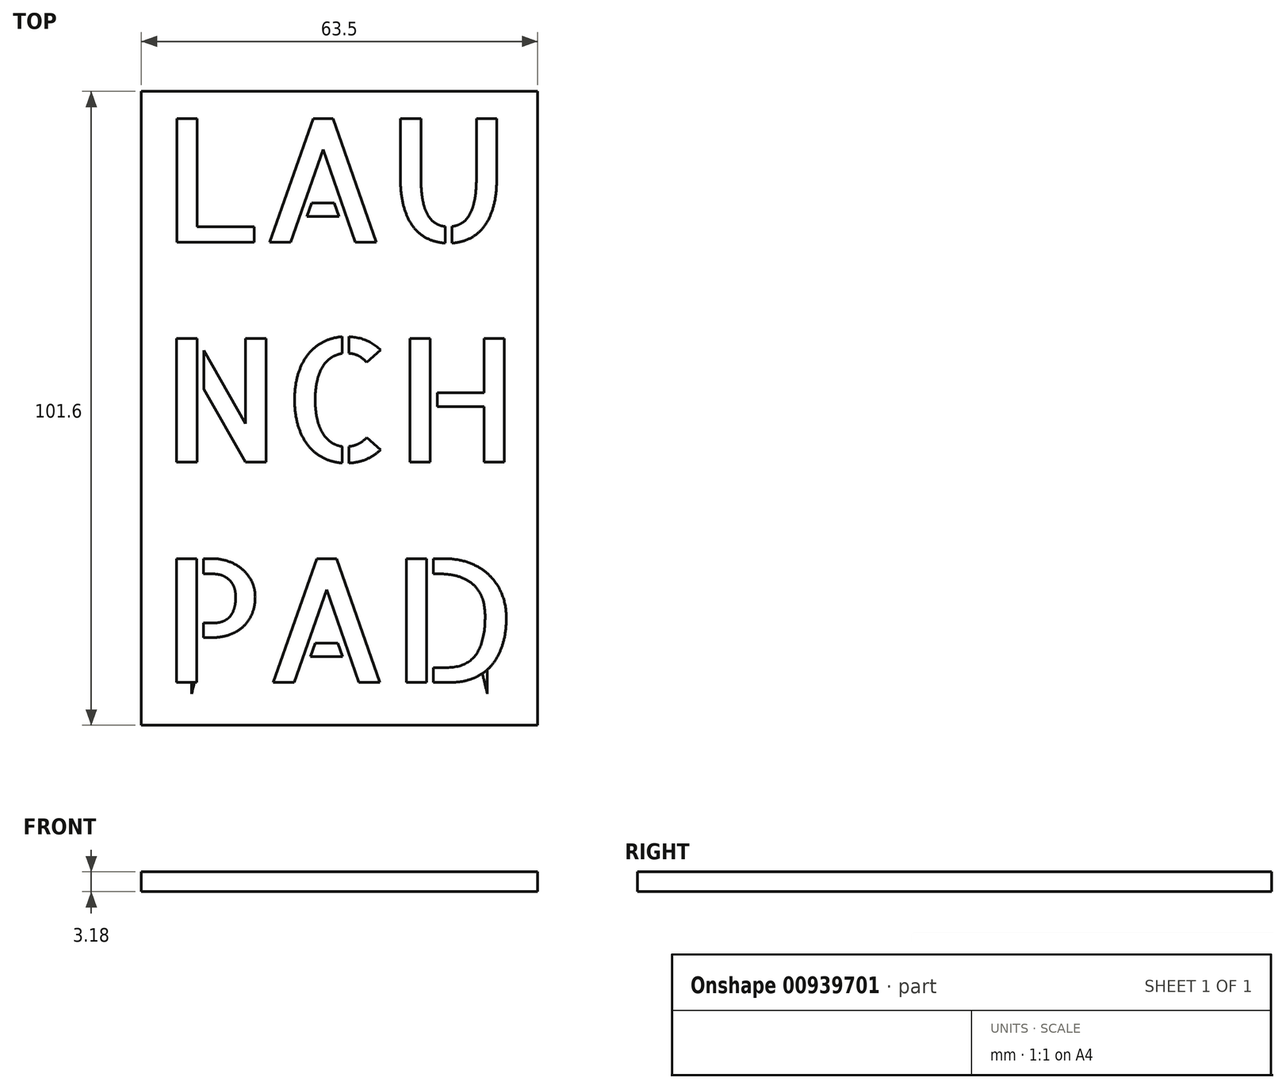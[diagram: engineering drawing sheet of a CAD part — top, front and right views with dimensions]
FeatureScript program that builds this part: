
annotation { "Feature Type Name" : "Feature", "Feature Type Description" : "" }
export const myFeature = defineFeature(function(context is Context, id is Id, definition is map)
    precondition{}
    {
        {
            var Q0;
            Q0=qCreatedBy(makeId("Top.planeOp"),FACE);
            var sketch = newSketch(context, id + "F0", { "sketchPlane" : qUnion([Q0])});
            skLineSegment(sketch, "E0.bottom", {"start": v(-31.75, 50.8) * mm, "end": v(31.75, 50.8) * mm});
            skLineSegment(sketch, "E0.top", {"start": v(-31.75, -50.8) * mm, "end": v(31.75, -50.8) * mm});
            skLineSegment(sketch, "E0.left", {"start": v(-31.75, 50.8) * mm, "end": v(-31.75, -50.8) * mm});
            skLineSegment(sketch, "E0.right", {"start": v(31.75, 50.8) * mm, "end": v(31.75, -50.8) * mm});
            skSolve(sketch);
        }
        {
            var Q0;
            Q0=makeQuery(id+"F0.imprint","IMPRINT",FACE,{"disambiguationData":[TD([[makeQuery(id+"F0.imprint","IMPRINT",EDGE,{"derivedFrom":sQuery(id+"F0.wireOp",EDGE,"E0.bottom")}),-1.0]])]});
            extrude(context, id + "F1", {"entities" : qUnion([Q0]), "depth" : 3.17 * mm, "offsetDistance" : 25.4 * mm});
        }
        {
            var Q0;
            Q0=makeQuery(id+"F1.opExtrude","CAP_FACE",FACE,{"disambiguationData":[OSD([sQuery(id+"F0.wireOp",EDGE,"E0.bottom"),sQuery(id+"F0.wireOp",EDGE,"E0.top"),sQuery(id+"F0.wireOp",EDGE,"E0.left"),sQuery(id+"F0.wireOp",EDGE,"E0.right")])],"isStart":false});
            var sketch = newSketch(context, id + "F2", { "sketchPlane" : qUnion([Q0])});
            skText(sketch, "E1", { "text": "LAU\nNCH\nPAD", "fontName": "AllertaStencil-Regular.ttf"});
            const initialGuessF2  = {"E1": [-0.02858, 0.02662, 1, 0, 0.01984]};
            skSetInitialGuess(sketch, initialGuessF2);
            skSolve(sketch);
        }
        {
            var Q0;
            Q0 = qSketchRegion(id + "F2", true);
            extrude(context, id + "F3", {"entities" : qUnion([Q0]), "operationType" : NewBodyOperationType.ADD, "depth" : 3 / 812.8 * mm, "offsetDistance" : 25.4 * mm});
        }
        {
            var Q0;
            {var subQ0=sQuery(id+"F0.wireOp",EDGE,"E0.top");var subQ1=sQuery(id+"F0.wireOp",EDGE,"E0.right");var subQ2=sQuery(id+"F0.wireOp",EDGE,"E0.bottom");var subQ3=sQuery(id+"F0.wireOp",EDGE,"E0.left");Q0=makeQuery(id+"F3.boolean.opBoolean","SPLIT",FACE,{"disambiguationData":[TD([makeQuery(id+"F1.opExtrude","SWEPT_FACE",FACE,{"disambiguationData":[OSD([subQ2])]})])],"derivedFrom":makeQuery(id+"F1.opExtrude","CAP_FACE",FACE,{"disambiguationData":[OSD([subQ2,subQ0,subQ3,subQ1])],"isStart":false})});}
            var sketch = newSketch(context, id + "F4", { "sketchPlane" : qUnion([Q0])});
            skPoint(sketch, "E2.1.internal.snap0", {"position": v(-24.46, 11.18) * mm});
            skPoint(sketch, "E3.2.internal.snap0", {"position": v(-2.05, -39.82) * mm});
            skFitSpline(sketch, "E4", {"points": [v(-5.95, -27.35) * mm, v(-8.13, -33.72) * mm, v(-5.95, -44.95) * mm], "startDerivative": vector(-6.61, -13.3) * mm, "endDerivative": vector(6.04, -21.2) * mm});
            skFitSpline(sketch, "E5", {"points": [v(-5.95, -44.95) * mm, v(-4.62, -39.82) * mm, v(0, -49.1) * mm], "startDerivative": vector(2.52, 18.1) * mm, "endDerivative": vector(9.23, -24.14) * mm});
            skFitSpline(sketch, "E6.MirrorCS", {"points": [v(5.95, -44.95) * mm, v(4.62, -39.82) * mm, v(0, -49.1) * mm], "startDerivative": vector(-2.52, 18.1) * mm, "endDerivative": vector(-9.23, -24.14) * mm});
            skFitSpline(sketch, "E7.MirrorCS", {"points": [v(5.95, -27.35) * mm, v(8.13, -33.72) * mm, v(5.95, -44.95) * mm], "startDerivative": vector(6.61, -13.3) * mm, "endDerivative": vector(-6.04, -21.2) * mm});
            skEllipticalArc(sketch, "E8", {});
            skLineSegment(sketch, "E9", {"start": v(-5.95, -27.35) * mm, "end": v(5.95, -27.35) * mm});
            skFitSpline(sketch, "E10", {"points": [v(-11.7, -12.15) * mm, v(-20.42, -19.2) * mm, v(-23.68, -45.79) * mm], "startDerivative": vector(-25.64, -12.83) * mm, "endDerivative": vector(-0.24, -51.69) * mm});
            skFitSpline(sketch, "E11", {"points": [v(-23.68, -45.79) * mm, v(-17.31, -29.12) * mm, v(-7.77, -24.5) * mm], "startDerivative": vector(8.28, 34.86) * mm, "endDerivative": vector(24.24, 6.48) * mm});
            skFitSpline(sketch, "E12.MirrorCS", {"points": [v(11.7, -12.15) * mm, v(20.42, -19.2) * mm, v(23.68, -45.79) * mm], "startDerivative": vector(25.64, -12.83) * mm, "endDerivative": vector(0.24, -51.69) * mm});
            skFitSpline(sketch, "E13.MirrorCS", {"points": [v(23.68, -45.79) * mm, v(17.31, -29.12) * mm, v(7.77, -24.5) * mm], "startDerivative": vector(-8.28, 34.86) * mm, "endDerivative": vector(-24.24, 6.48) * mm});
            const initialGuessF4  = {"E8": [0, 0, 0, -1, 0.030929374872957237, 0.012728021231775851, 0.4860810952605146, 5.797104211919072]};
            skSetInitialGuess(sketch, initialGuessF4);
            skSolve(sketch);
        }
        {
            var Q0;
            {var subQ1=makeQuery(id+"F3.opExtrude","CAP_EDGE",EDGE,{"disambiguationData":[OSD([sQuery(id+"F2.wireOp",EDGE,"E1.sketch_text.stroke-6")])],"isStart":true});Q0=makeQuery(id+"F4.imprint","IMPRINT",FACE,{"disambiguationData":[TD([[makeQuery(id+"F4.imprint","IMPRINT",EDGE,{"derivedFrom":subQ1}),1.0]])]});}
            var Q1;
            Q1=makeQuery(id+"F4.imprint","IMPRINT",FACE,{"disambiguationData":[TD([[makeQuery(id+"F4.imprint","IMPRINT",EDGE,{"derivedFrom":makeQuery(id+"F3.opExtrude","CAP_EDGE",EDGE,{"disambiguationData":[OSD([sQuery(id+"F2.wireOp",EDGE,"E1.sketch_text.stroke-97")])],"isStart":true})}),1.0]])]});
            var Q2;
            {var subQ9=makeQuery(id+"F3.opExtrude","CAP_EDGE",EDGE,{"disambiguationData":[OSD([sQuery(id+"F2.wireOp",EDGE,"E1.sketch_text.stroke-130")])],"isStart":true});Q2=makeQuery(id+"F4.imprint","IMPRINT",FACE,{"disambiguationData":[TD([[makeQuery(id+"F4.imprint","IMPRINT",EDGE,{"derivedFrom":subQ9}),1.0]])]});}
            var Q3;
            {var subQ12=makeQuery(id+"F3.opExtrude","CAP_EDGE",EDGE,{"disambiguationData":[OSD([sQuery(id+"F2.wireOp",EDGE,"E1.sketch_text.stroke-126")])],"isStart":true});Q3=makeQuery(id+"F4.imprint","IMPRINT",FACE,{"disambiguationData":[TD([[makeQuery(id+"F4.imprint","IMPRINT",EDGE,{"derivedFrom":subQ12}),1.0]])]});}
            var Q4;
            {var subQ1=sQuery(id+"F4.wireOp",EDGE,"E7.MirrorCS");var subQ3=makeQuery(id+"F3.opExtrude","CAP_EDGE",EDGE,{"disambiguationData":[OSD([sQuery(id+"F2.wireOp",EDGE,"E1.sketch_text.stroke-125")])],"isStart":true});var subQ4=makeQuery(id+"F4.imprint","INTERSECT",VERTEX,{"derivedFrom":[subQ3,subQ1]});Q4=makeQuery(id+"F4.imprint","IMPRINT",FACE,{"disambiguationData":[TD([[makeQuery(id+"F4.imprint","IMPRINT",EDGE,{"disambiguationData":[TD([[subQ4,1.0]])],"derivedFrom":subQ3}),1.0]])]});}
            var Q5;
            {var subQ1=sQuery(id+"F4.wireOp",EDGE,"E4");var subQ3=makeQuery(id+"F3.opExtrude","CAP_EDGE",EDGE,{"disambiguationData":[OSD([sQuery(id+"F2.wireOp",EDGE,"E1.sketch_text.stroke-123")])],"isStart":true});var subQ4=makeQuery(id+"F4.imprint","INTERSECT",VERTEX,{"derivedFrom":[subQ3,subQ1]});Q5=makeQuery(id+"F4.imprint","IMPRINT",FACE,{"disambiguationData":[TD([[makeQuery(id+"F4.imprint","IMPRINT",EDGE,{"disambiguationData":[TD([[subQ4,-1.0]])],"derivedFrom":subQ3}),1.0]])]});}
            var Q6;
            {var subQ0=sQuery(id+"F4.wireOp",EDGE,"E13.MirrorCS");var subQ1=sQuery(id+"F4.wireOp",EDGE,"E12.MirrorCS");var subQ2=makeQuery(id+"F4.imprint","INTERSECT",VERTEX,{"derivedFrom":[subQ1,subQ0]});Q6=makeQuery(id+"F4.imprint","IMPRINT",FACE,{"disambiguationData":[TD([[makeQuery(id+"F4.imprint","IMPRINT",EDGE,{"disambiguationData":[TD([[subQ2,1.0]])],"derivedFrom":subQ1}),-1.0]])]});}
            var Q7;
            {var subQ0=sQuery(id+"F4.wireOp",EDGE,"E11");var subQ1=sQuery(id+"F4.wireOp",EDGE,"E10");var subQ2=makeQuery(id+"F4.imprint","INTERSECT",VERTEX,{"derivedFrom":[subQ1,subQ0]});Q7=makeQuery(id+"F4.imprint","IMPRINT",FACE,{"disambiguationData":[TD([[makeQuery(id+"F4.imprint","IMPRINT",EDGE,{"disambiguationData":[TD([[subQ2,1.0]])],"derivedFrom":subQ1}),1.0]])]});}
            extrude(context, id + "F5", {"entities" : qUnion([Q0, Q1, Q2, Q3, Q4, Q5, Q6, Q7]), "operationType" : NewBodyOperationType.ADD, "depth" : 1 / 406.4 * mm, "offsetDistance" : 25.4 * mm});
        }
    });
